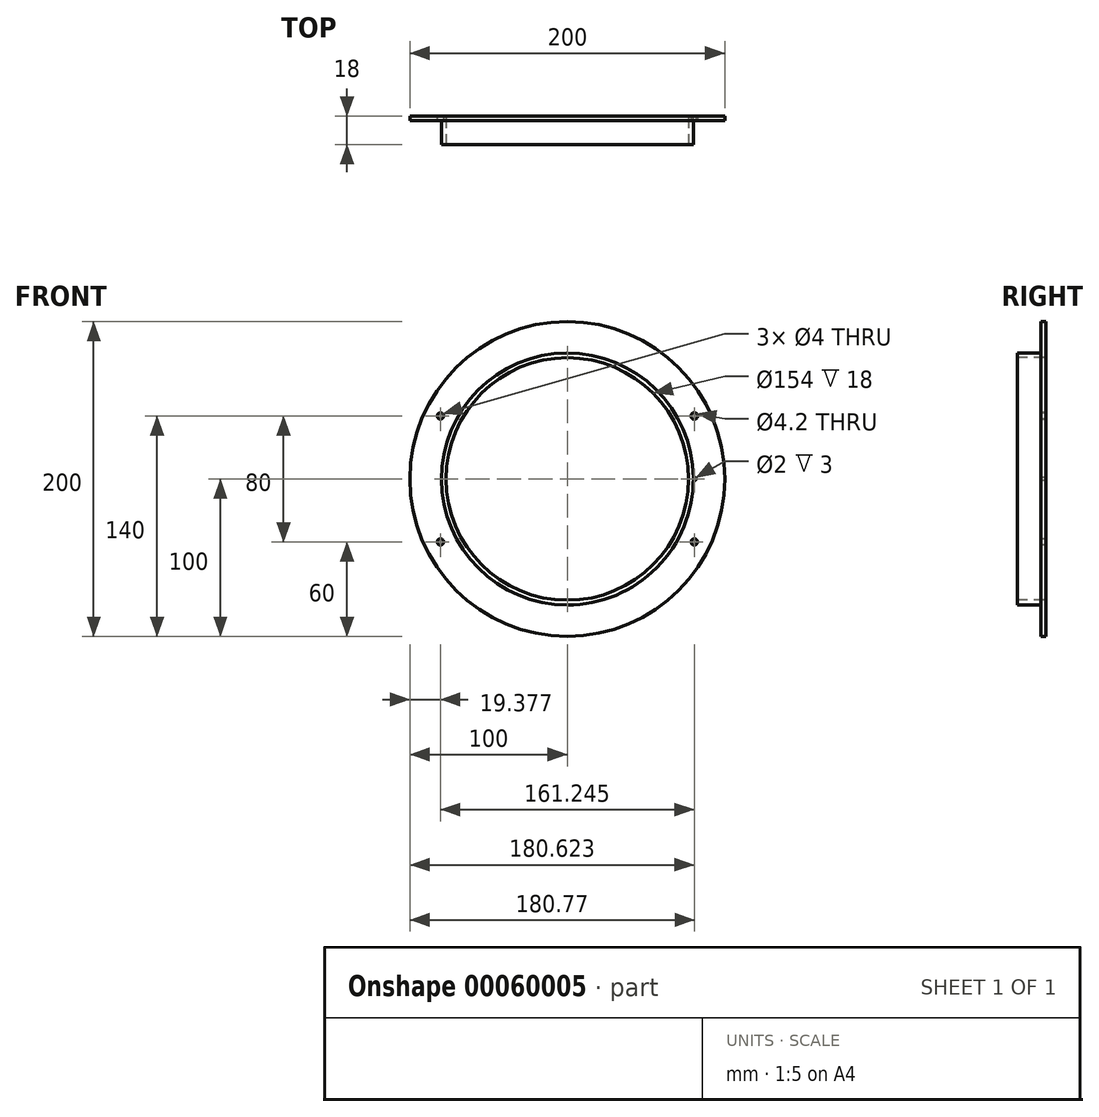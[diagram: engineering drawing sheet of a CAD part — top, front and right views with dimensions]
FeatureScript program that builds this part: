
annotation { "Feature Type Name" : "Feature", "Feature Type Description" : "" }
export const myFeature = defineFeature(function(context is Context, id is Id, definition is map)
    precondition{}
    {
        {
            var Q0;
            Q0=qCreatedBy(makeId("Front.planeOp"),FACE);
            var sketch = newSketch(context, id + "F0", { "sketchPlane" : qUnion([Q0])});
            skCircle(sketch, "E0", {"center": v(0, 0) * mm, "radius": 100 * mm});
            skSolve(sketch);
        }
        {
            var Q0;
            Q0=qSketchRegion(id+"F0",true);
            extrude(context, id + "F1", {"entities" : qUnion([Q0]), "depth" : 3 * mm});
        }
        {
            var Q0;
            Q0=makeQuery(id+"F1.opExtrude","CAP_FACE",FACE,{"disambiguationData":[OSD([sQuery(id+"F0.wireOp",EDGE,"E0")])],"isStart":false});
            var sketch = newSketch(context, id + "F2", { "sketchPlane" : qUnion([Q0])});
            skCircle(sketch, "E1", {"center": v(0, 0) * mm, "radius": 80 * mm});
            skSolve(sketch);
        }
        {
            var Q0;
            Q0=qSketchRegion(id+"F2",true);
            extrude(context, id + "F3", {"entities" : qUnion([Q0]), "operationType" : NewBodyOperationType.ADD, "depth" : 15 * mm});
        }
        {
            var Q0;
            Q0=makeQuery(id+"F3.opExtrude","CAP_FACE",FACE,{"disambiguationData":[OSD([sQuery(id+"F2.wireOp",EDGE,"E1")])],"isStart":false});
            var sketch = newSketch(context, id + "F4", { "sketchPlane" : qUnion([Q0])});
            skCircle(sketch, "E2", {"center": v(0, 0) * mm, "radius": 77 * mm});
            skSolve(sketch);
        }
        {
            var Q0;
            Q0=qSketchRegion(id+"F4",true);
            extrude(context, id + "F5", {"entities" : qUnion([Q0]), "operationType" : NewBodyOperationType.REMOVE, "endBound" : BoundingType.THROUGH_ALL, "oppositeDirection" : true, "depth" : 25 * mm});
        }
        {
            var Q0;
            Q0=makeQuery(id+"F1.opExtrude","CAP_FACE",FACE,{"disambiguationData":[OSD([sQuery(id+"F0.wireOp",EDGE,"E0")])],"isStart":false});
            var sketch = newSketch(context, id + "F6", { "sketchPlane" : qUnion([Q0])});
            skCircle(sketch, "E3", {"center": v(80.62, 40) * mm, "radius": 2.1 * mm});
            skCircle(sketch, "E4", {"center": v(-80.62, 40) * mm, "radius": 2 * mm});
            skCircle(sketch, "E5", {"center": v(-80.62, -40) * mm, "radius": 2 * mm});
            skCircle(sketch, "E6", {"center": v(80.62, -40) * mm, "radius": 2 * mm});
            skCircle(sketch, "E7", {"center": v(80.77, 0) * mm, "radius": 1 * mm});
            skSolve(sketch);
        }
        {
            var Q0;
            Q0 = qSketchRegion(id + "F6", true);
            extrude(context, id + "F7", {"entities" : qUnion([Q0]), "operationType" : NewBodyOperationType.REMOVE, "endBound" : BoundingType.THROUGH_ALL, "oppositeDirection" : true, "depth" : 25 * mm});
        }
    });
